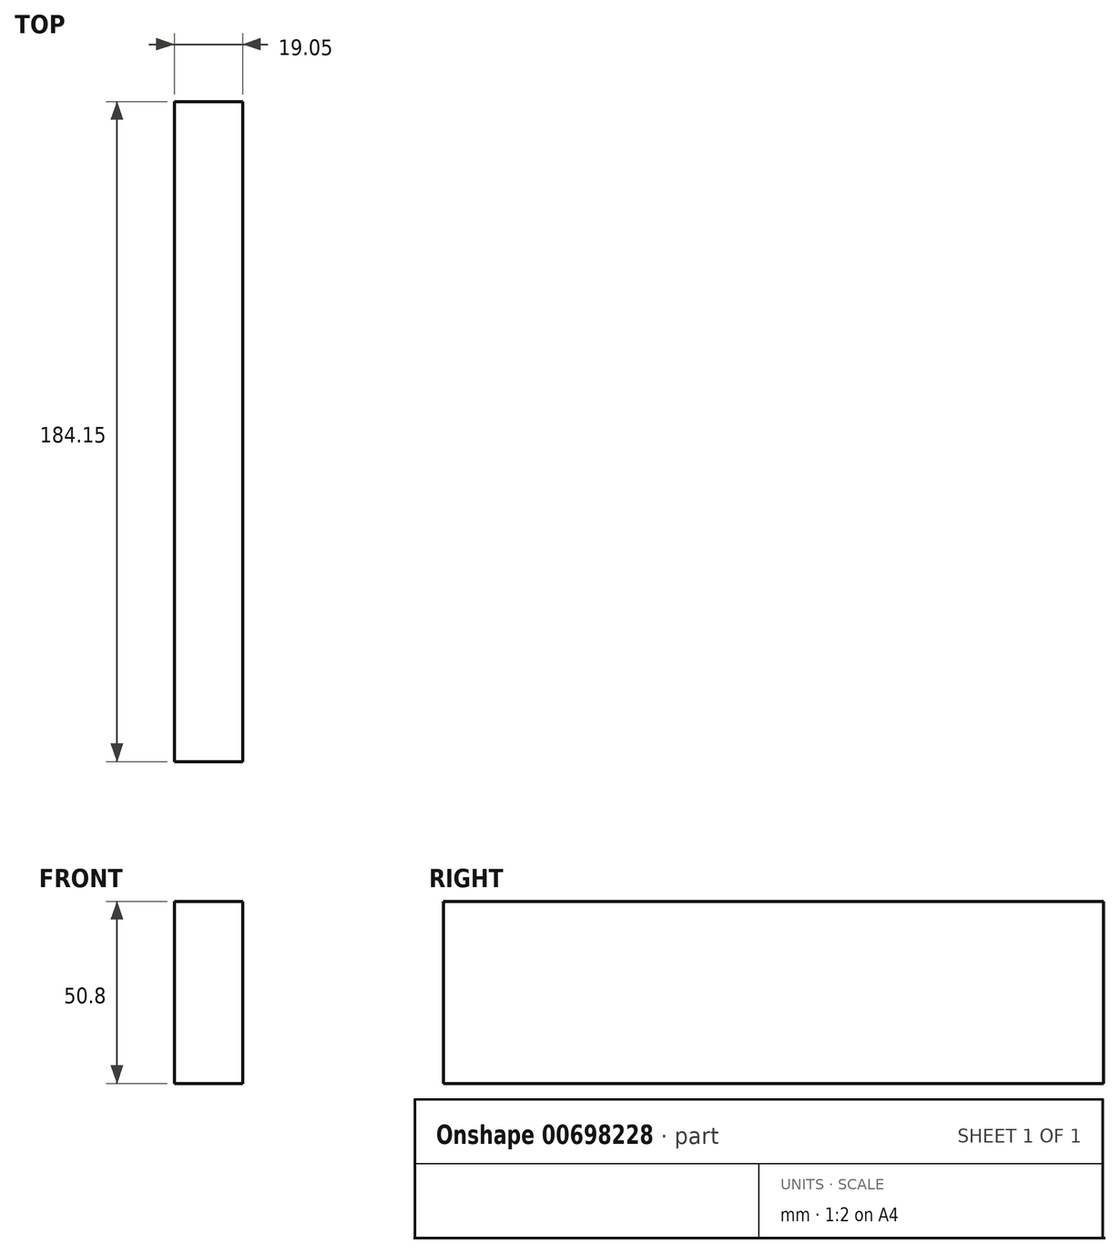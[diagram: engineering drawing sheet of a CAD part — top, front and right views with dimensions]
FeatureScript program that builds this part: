
annotation { "Feature Type Name" : "Feature", "Feature Type Description" : "" }
export const myFeature = defineFeature(function(context is Context, id is Id, definition is map)
    precondition{}
    {
        {
            var Q0;
            Q0=qCreatedBy(makeId("Top.planeOp"),FACE);
            var sketch = newSketch(context, id + "F0", { "sketchPlane" : qUnion([Q0])});
            skLineSegment(sketch, "E0.bottom", {"start": v(-115.52, 0) * mm, "end": v(-96.47, 0) * mm});
            skLineSegment(sketch, "E0.top", {"start": v(-115.52, 184.15) * mm, "end": v(-96.47, 184.15) * mm});
            skLineSegment(sketch, "E0.left", {"start": v(-115.52, 0) * mm, "end": v(-115.52, 184.15) * mm});
            skLineSegment(sketch, "E0.right", {"start": v(-96.47, 0) * mm, "end": v(-96.47, 184.15) * mm});
            skSolve(sketch);
        }
        {
            var Q0;
            Q0=makeQuery(id+"F0.imprint","IMPRINT",FACE,{"disambiguationData":[TD([[makeQuery(id+"F0.imprint","IMPRINT",EDGE,{"derivedFrom":sQuery(id+"F0.wireOp",EDGE,"E0.bottom")}),1.0]])]});
            extrude(context, id + "F1", {"entities" : qUnion([Q0]), "depth" : 50.8 * mm, "offsetDistance" : 25.4 * mm});
        }
    });
